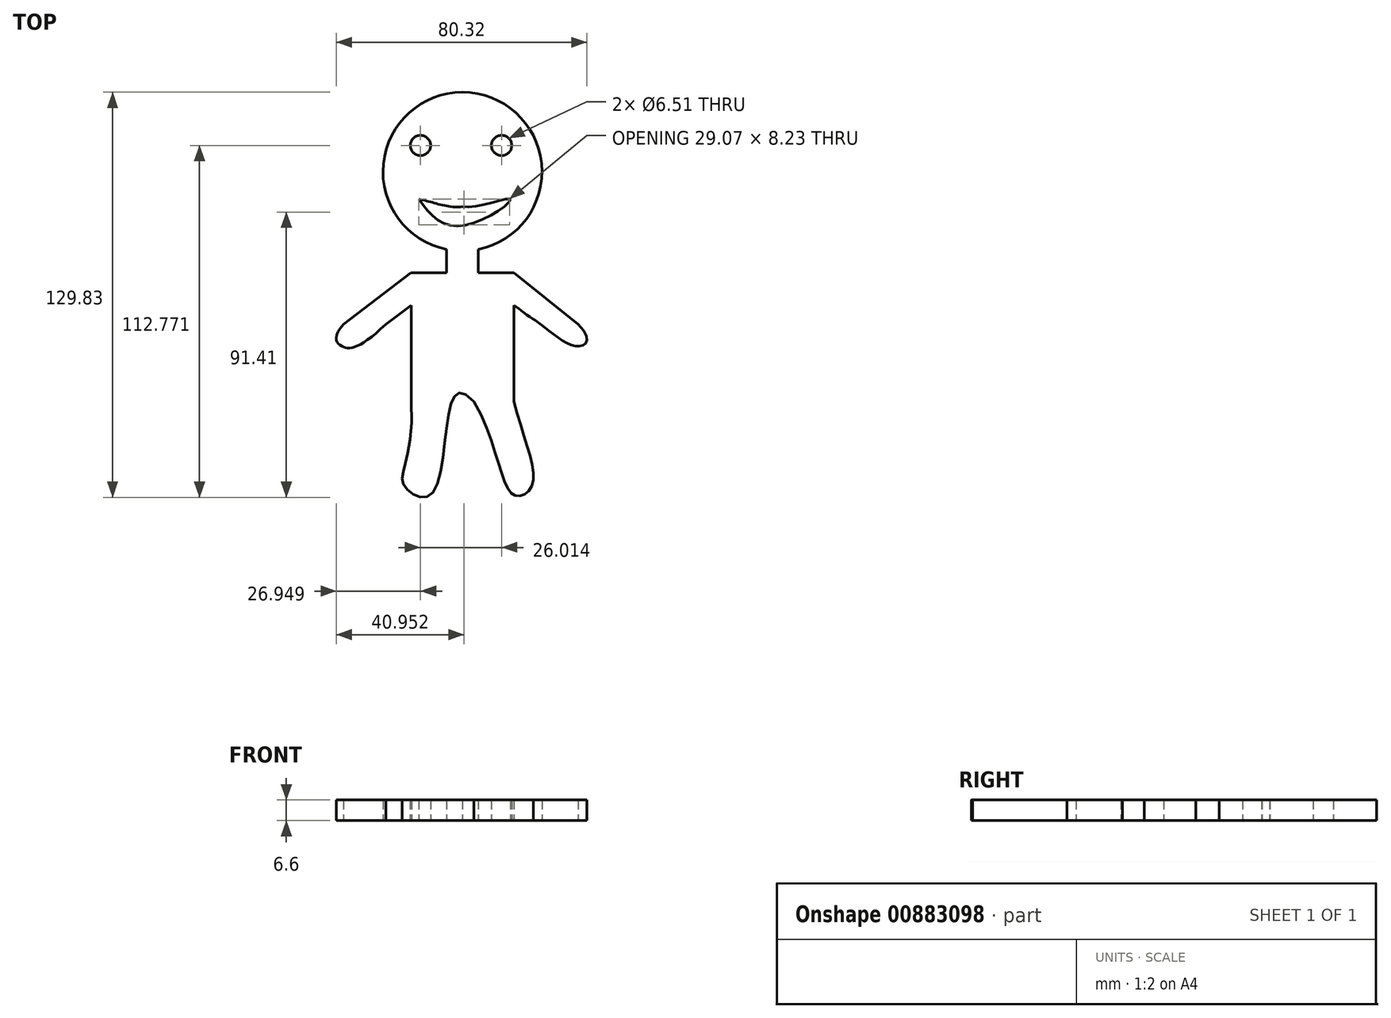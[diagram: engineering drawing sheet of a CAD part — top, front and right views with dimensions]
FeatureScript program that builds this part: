
annotation { "Feature Type Name" : "Feature", "Feature Type Description" : "" }
export const myFeature = defineFeature(function(context is Context, id is Id, definition is map)
    precondition{}
    {
        {
            var Q0;
            Q0=qCreatedBy(makeId("Top.planeOp"),FACE);
            var sketch = newSketch(context, id + "F0", { "sketchPlane" : qUnion([Q0])});
            skArc(sketch, "E0", {"start": v(5.1, 24.03) * mm, "mid": v(0, 74.43) * mm, "end": v(-5.09, 24.03) * mm});
            skLineSegment(sketch, "E1", {"start": v(-5.09, 24.03) * mm, "end": v(-5.09, 16.51) * mm});
            skLineSegment(sketch, "E2", {"start": v(-5.09, 16.51) * mm, "end": v(-16.5, 16.51) * mm});
            skLineSegment(sketch, "E3", {"start": v(5.1, 24.03) * mm, "end": v(5.1, 16.51) * mm});
            skLineSegment(sketch, "E4", {"start": v(5.1, 16.51) * mm, "end": v(16.5, 16.51) * mm});
            skLineSegment(sketch, "E5", {"start": v(-16.5, 16.51) * mm, "end": v(-38.15, 0) * mm});
            skLineSegment(sketch, "E6", {"start": v(-24.58, 0) * mm, "end": v(-16.44, 6.2) * mm});
            skFitSpline(sketch, "E7", {"points": [v(-38.15, 0) * mm, v(-38.54, -7) * mm, v(-24.58, 0) * mm], "startDerivative": vector(-27.45, -31.02) * mm, "endDerivative": vector(39.93, 37.4) * mm});
            skLineSegment(sketch, "E8", {"start": v(-16.44, 6.2) * mm, "end": v(-16.44, -24.73) * mm});
            skFitSpline(sketch, "E9", {"points": [v(-16.44, -24.73) * mm, v(-18.61, -51.73) * mm, v(-10.33, -54.69) * mm, v(-3.42, -24.73) * mm, v(3.68, -24.73) * mm], "startDerivative": vector(11.05, -173.05) * mm, "endDerivative": vector(67.91, -76.82) * mm});
            skFitSpline(sketch, "E10", {"points": [v(3.68, -24.73) * mm, v(16.5, -54.69) * mm, v(22.23, -51.73) * mm, v(16.5, -24.73) * mm], "startDerivative": vector(55.66, -96.47) * mm, "endDerivative": vector(-21, 86.6) * mm});
            skLineSegment(sketch, "E11", {"start": v(16.5, -24.73) * mm, "end": v(16.5, 6.2) * mm});
            skLineSegment(sketch, "E12", {"start": v(16.5, 16.51) * mm, "end": v(37.03, 0) * mm});
            skFitSpline(sketch, "E13", {"points": [v(37.03, 0) * mm, v(37.03, -7) * mm, v(25.2, 0) * mm, v(16.5, 6.2) * mm], "startDerivative": vector(52.76, -51.06) * mm, "endDerivative": vector(-39.35, 32.17) * mm});
            skCircle(sketch, "E14", {"center": v(-13.46, 57.37) * mm, "radius": 3.26 * mm});
            skCircle(sketch, "E15", {"center": v(12.55, 57.37) * mm, "radius": 3.26 * mm});
            skFitSpline(sketch, "E16", {"points": [v(-14, 40.13) * mm, v(0, 37.78) * mm], "startDerivative": vector(9.89, -1.07) * mm, "endDerivative": vector(13.5, 2.62) * mm});
            skFitSpline(sketch, "E17", {"points": [v(0, 37.78) * mm, v(15.28, 40.13) * mm, v(0, 31.62) * mm, v(-14, 40.13) * mm], "startDerivative": vector(36.63, -9.74) * mm, "endDerivative": vector(-31.11, 43.69) * mm});
            skSolve(sketch);
        }
        {
            var Q0;
            Q0=makeQuery(id+"F0.imprint","IMPRINT",FACE,{"disambiguationData":[TD([[makeQuery(id+"F0.imprint","IMPRINT",EDGE,{"derivedFrom":sQuery(id+"F0.wireOp",EDGE,"E0")}),1.0]])]});
            var Q1;
            Q1=sQuery(id+"F0.wireOp",EDGE,"E0");
            var Q2;
            Q2=sQuery(id+"F0.wireOp",EDGE,"E2");
            var Q3;
            Q3=sQuery(id+"F0.wireOp",EDGE,"E1");
            var Q4;
            Q4=sQuery(id+"F0.wireOp",EDGE,"E3");
            var Q5;
            Q5=sQuery(id+"F0.wireOp",EDGE,"E4");
            var Q6;
            Q6=sQuery(id+"F0.wireOp",EDGE,"22b5db82-bc98-4e5b-b947-5d4af7a17cd4");
            extrude(context, id + "F1", {"entities" : qUnion([Q0]), "surfaceOperationType" : NewSurfaceOperationType.ADD, "surfaceEntities" : qUnion([Q1, Q2, Q3, Q4, Q5, Q6]), "endBound" : BoundingType.SYMMETRIC, "depth" : 6.6 * mm, "offsetDistance" : 25.4 * mm});
        }
    });
